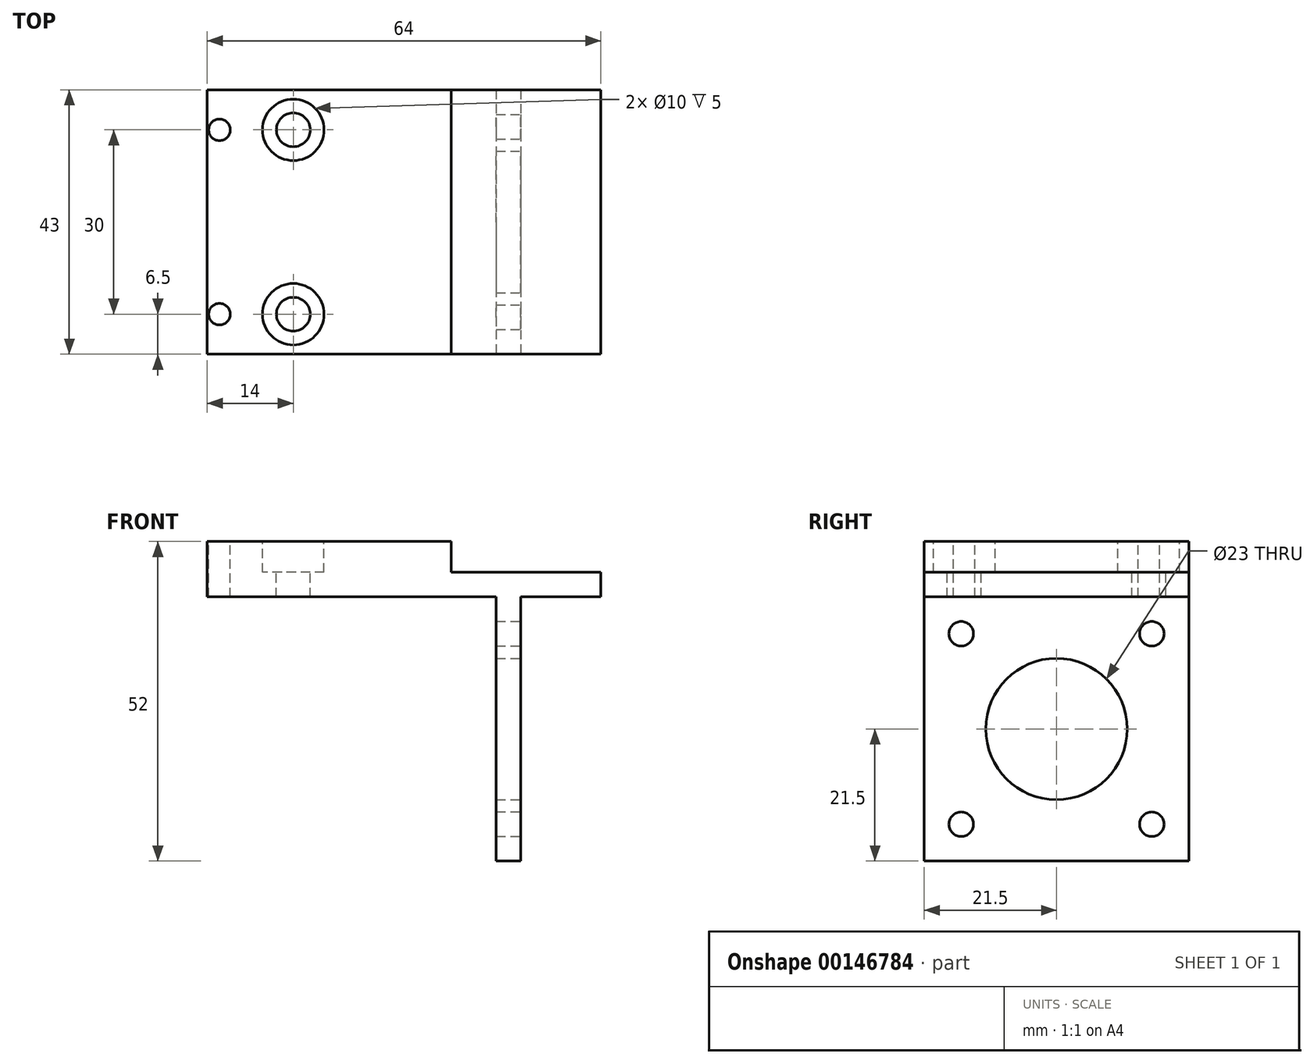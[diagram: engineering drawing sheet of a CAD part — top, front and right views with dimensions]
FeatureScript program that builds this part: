
annotation { "Feature Type Name" : "Feature", "Feature Type Description" : "" }
export const myFeature = defineFeature(function(context is Context, id is Id, definition is map)
    precondition{}
    {
        {
            var Q0;
            Q0=qCreatedBy(makeId("Top.planeOp"),FACE);
            var sketch = newSketch(context, id + "F0", { "sketchPlane" : qUnion([Q0])});
            skLineSegment(sketch, "E0.bottom", {"start": v(32, -21.5) * mm, "end": v(-32, -21.5) * mm});
            skLineSegment(sketch, "E0.top", {"start": v(32, 21.5) * mm, "end": v(-32, 21.5) * mm});
            skLineSegment(sketch, "E0.left", {"start": v(32, -21.5) * mm, "end": v(32, 21.5) * mm});
            skLineSegment(sketch, "E0.right", {"start": v(-32, -21.5) * mm, "end": v(-32, 21.5) * mm});
            skPoint(sketch, "E0.middle", {"position": v(0, 0) * mm});
            skSolve(sketch);
        }
        {
            var Q0;
            Q0=makeQuery(id+"F0.imprint","IMPRINT",FACE,{"disambiguationData":[TD([[makeQuery(id+"F0.imprint","IMPRINT",EDGE,{"derivedFrom":sQuery(id+"F0.wireOp",EDGE,"E0.bottom")}),-1.0]])]});
            extrude(context, id + "F8", {"entities" : qUnion([Q0]), "depth" : 4 * mm});
        }
        {
            var Q0;
            Q0=makeQuery(id+"F8.opExtrude","CAP_FACE",FACE,{"disambiguationData":[OSD([sQuery(id+"F0.wireOp",EDGE,"E0.bottom"),sQuery(id+"F0.wireOp",EDGE,"E0.top"),sQuery(id+"F0.wireOp",EDGE,"E0.left"),sQuery(id+"F0.wireOp",EDGE,"E0.right")])],"isStart":true});
            var sketch = newSketch(context, id + "F1", { "sketchPlane" : qUnion([Q0])});
            skLineSegment(sketch, "E1.bottom", {"start": v(19, -21.5) * mm, "end": v(15, -21.5) * mm});
            skLineSegment(sketch, "E1.top", {"start": v(19, 21.5) * mm, "end": v(15, 21.5) * mm});
            skLineSegment(sketch, "E1.left", {"start": v(19, -21.5) * mm, "end": v(19, 21.5) * mm});
            skLineSegment(sketch, "E1.right", {"start": v(15, -21.5) * mm, "end": v(15, 21.5) * mm});
            skSolve(sketch);
        }
        {
            var Q0;
            Q0 = qSketchRegion(id + "F1", true);
            extrude(context, id + "F2", {"entities" : qUnion([Q0]), "operationType" : NewBodyOperationType.ADD, "depth" : 43 * mm});
        }
        {
            var Q0;
            Q0=makeQuery(id+"F2.opExtrude","SWEPT_FACE",FACE,{"disambiguationData":[OSD([sQuery(id+"F1.wireOp",EDGE,"E1.left")])]});
            var sketch = newSketch(context, id + "F3", { "sketchPlane" : qUnion([Q0])});
            skLineSegment(sketch, "E2.bottom", {"start": v(-15.5, -37) * mm, "end": v(15.5, -37) * mm});
            skLineSegment(sketch, "E2.top", {"start": v(-15.5, -6) * mm, "end": v(15.5, -6) * mm});
            skLineSegment(sketch, "E2.left", {"start": v(-15.5, -37) * mm, "end": v(-15.5, -6) * mm});
            skLineSegment(sketch, "E2.right", {"start": v(15.5, -37) * mm, "end": v(15.5, -6) * mm});
            skPoint(sketch, "E2.middle", {"position": v(0, -21.5) * mm});
            skPoint(sketch, "E2.middle.positionSnap0", {"position": v(0, -43) * mm});
            skPoint(sketch, "E2.middle.positionSnap1", {"position": v(21.5, -21.5) * mm});
            skPoint(sketch, "E2.centerSnap0", {"position": v(0, -43) * mm});
            skPoint(sketch, "E2.centerSnap1", {"position": v(21.5, -21.5) * mm});
            skSolve(sketch);
        }
        {
            var Q0;
            Q0=sQuery(id+"F3.wireOp",VERTEX,"E2.right.start");
            var Q1;
            Q1=sQuery(id+"F3.wireOp",VERTEX,"E2.top.end");
            var Q2;
            Q2=sQuery(id+"F3.wireOp",VERTEX,"E2.left.start");
            var Q3;
            Q3=sQuery(id+"F3.wireOp",VERTEX,"E2.top.start");
            var Q4;
            Q4=makeQuery(id+"F8.opExtrude","SWEPT_BODY",BODY,{"disambiguationData":[OSD([sQuery(id+"F0.wireOp",EDGE,"E0.bottom"),sQuery(id+"F0.wireOp",EDGE,"E0.top"),sQuery(id+"F0.wireOp",EDGE,"E0.left"),sQuery(id+"F0.wireOp",EDGE,"E0.right")])]});
            hole(context, id + "F4", {"style" : HoleStyle.SIMPLE, "endStyle" : HoleEndStyle.THROUGH, "holeDiameter" : 4 * mm, "locations" : qUnion([Q0, Q1, Q2, Q3]), "scope" : qUnion([Q4]), "isTappedThrough" : true});
        }
        {
            var Q0;
            Q0=sQuery(id+"F3.wireOp",VERTEX,"E2.middle");
            var Q1;
            Q1=makeQuery(id+"F8.opExtrude","SWEPT_BODY",BODY,{"disambiguationData":[OSD([sQuery(id+"F0.wireOp",EDGE,"E0.bottom"),sQuery(id+"F0.wireOp",EDGE,"E0.top"),sQuery(id+"F0.wireOp",EDGE,"E0.left"),sQuery(id+"F0.wireOp",EDGE,"E0.right")])]});
            hole(context, id + "F9", {"style" : HoleStyle.SIMPLE, "endStyle" : HoleEndStyle.THROUGH, "holeDiameter" : 23 * mm, "locations" : qUnion([Q0]), "scope" : qUnion([Q1]), "isTappedThrough" : true});
        }
        {
            var Q0;
            Q0=makeQuery(id+"F8.opExtrude","CAP_FACE",FACE,{"disambiguationData":[OSD([sQuery(id+"F0.wireOp",EDGE,"E0.bottom"),sQuery(id+"F0.wireOp",EDGE,"E0.top"),sQuery(id+"F0.wireOp",EDGE,"E0.left"),sQuery(id+"F0.wireOp",EDGE,"E0.right")])],"isStart":false});
            var sketch = newSketch(context, id + "F5", { "sketchPlane" : qUnion([Q0])});
            skLineSegment(sketch, "E3.bottom", {"start": v(-32, -21.5) * mm, "end": v(7.66, -21.5) * mm});
            skLineSegment(sketch, "E3.top", {"start": v(-32, 21.5) * mm, "end": v(7.66, 21.5) * mm});
            skLineSegment(sketch, "E3.left", {"start": v(-32, -21.5) * mm, "end": v(-32, 21.5) * mm});
            skLineSegment(sketch, "E3.right", {"start": v(7.66, -21.5) * mm, "end": v(7.66, 21.5) * mm});
            skSolve(sketch);
        }
        {
            var Q0;
            Q0=makeQuery(id+"F5.imprint","IMPRINT",FACE,{"disambiguationData":[TD([[makeQuery(id+"F5.imprint","IMPRINT",EDGE,{"derivedFrom":sQuery(id+"F5.wireOp",EDGE,"E3.bottom")}),-1.0]])]});
            extrude(context, id + "F10", {"entities" : qUnion([Q0]), "operationType" : NewBodyOperationType.ADD, "depth" : 20 * mm});
        }
        {
            var Q0;
            Q0=makeQuery(id+"F10.opExtrude","CAP_FACE",FACE,{"disambiguationData":[OSD([sQuery(id+"F5.wireOp",EDGE,"E3.bottom"),sQuery(id+"F5.wireOp",EDGE,"E3.top"),sQuery(id+"F5.wireOp",EDGE,"E3.left"),sQuery(id+"F5.wireOp",EDGE,"E3.right")])],"isStart":false});
            var sketch = newSketch(context, id + "F6", { "sketchPlane" : qUnion([Q0])});
            skPoint(sketch, "E4", {"position": v(-18, 15) * mm});
            skPoint(sketch, "E5", {"position": v(-18, -15) * mm});
            skPoint(sketch, "E6", {"position": v(-30, 15) * mm});
            skPoint(sketch, "E7", {"position": v(-30, -15) * mm});
            skSolve(sketch);
        }
        {
            var Q0;
            Q0=sQuery(id+"F6.wireOp",VERTEX,"E5");
            var Q1;
            Q1=sQuery(id+"F6.wireOp",VERTEX,"E4");
            var Q2;
            Q2=makeQuery(id+"F8.opExtrude","SWEPT_BODY",BODY,{"disambiguationData":[OSD([sQuery(id+"F0.wireOp",EDGE,"E0.bottom"),sQuery(id+"F0.wireOp",EDGE,"E0.top"),sQuery(id+"F0.wireOp",EDGE,"E0.left"),sQuery(id+"F0.wireOp",EDGE,"E0.right")])]});
            hole(context, id + "F7", {"style" : HoleStyle.C_BORE, "endStyle" : HoleEndStyle.THROUGH, "holeDiameter" : 5.5 * mm, "cBoreDiameter" : 10 * mm, "cBoreDepth" : 20 * mm, "locations" : qUnion([Q0, Q1]), "scope" : qUnion([Q2]), "isTappedThrough" : true});
        }
        {
            var Q0;
            Q0=sQuery(id+"F6.wireOp",VERTEX,"E6");
            var Q1;
            Q1=sQuery(id+"F6.wireOp",VERTEX,"E7");
            var Q2;
            Q2=makeQuery(id+"F8.opExtrude","SWEPT_BODY",BODY,{"disambiguationData":[OSD([sQuery(id+"F0.wireOp",EDGE,"E0.bottom"),sQuery(id+"F0.wireOp",EDGE,"E0.top"),sQuery(id+"F0.wireOp",EDGE,"E0.left"),sQuery(id+"F0.wireOp",EDGE,"E0.right")])]});
            hole(context, id + "F11", {"style" : HoleStyle.C_BORE, "endStyle" : HoleEndStyle.THROUGH, "holeDiameter" : 3.5 * mm, "cBoreDiameter" : 5 * mm, "cBoreDepth" : 15 * mm, "locations" : qUnion([Q0, Q1]), "scope" : qUnion([Q2]), "isTappedThrough" : true});
        }
        {
            var Q0;
            Q0=makeQuery(id+"F6.imprint","IMPRINT",FACE,{"disambiguationData":[TD([[makeQuery(id+"F6.imprint","IMPRINT",EDGE,{"derivedFrom":makeQuery(id+"F10.opExtrude","CAP_EDGE",EDGE,{"disambiguationData":[OSD([sQuery(id+"F5.wireOp",EDGE,"E3.bottom")])],"isStart":false})}),-1.0]])]});
            extrude(context, id + "F12", {"entities" : qUnion([Q0]), "operationType" : NewBodyOperationType.REMOVE, "oppositeDirection" : true, "depth" : 15 * mm});
        }
    });
